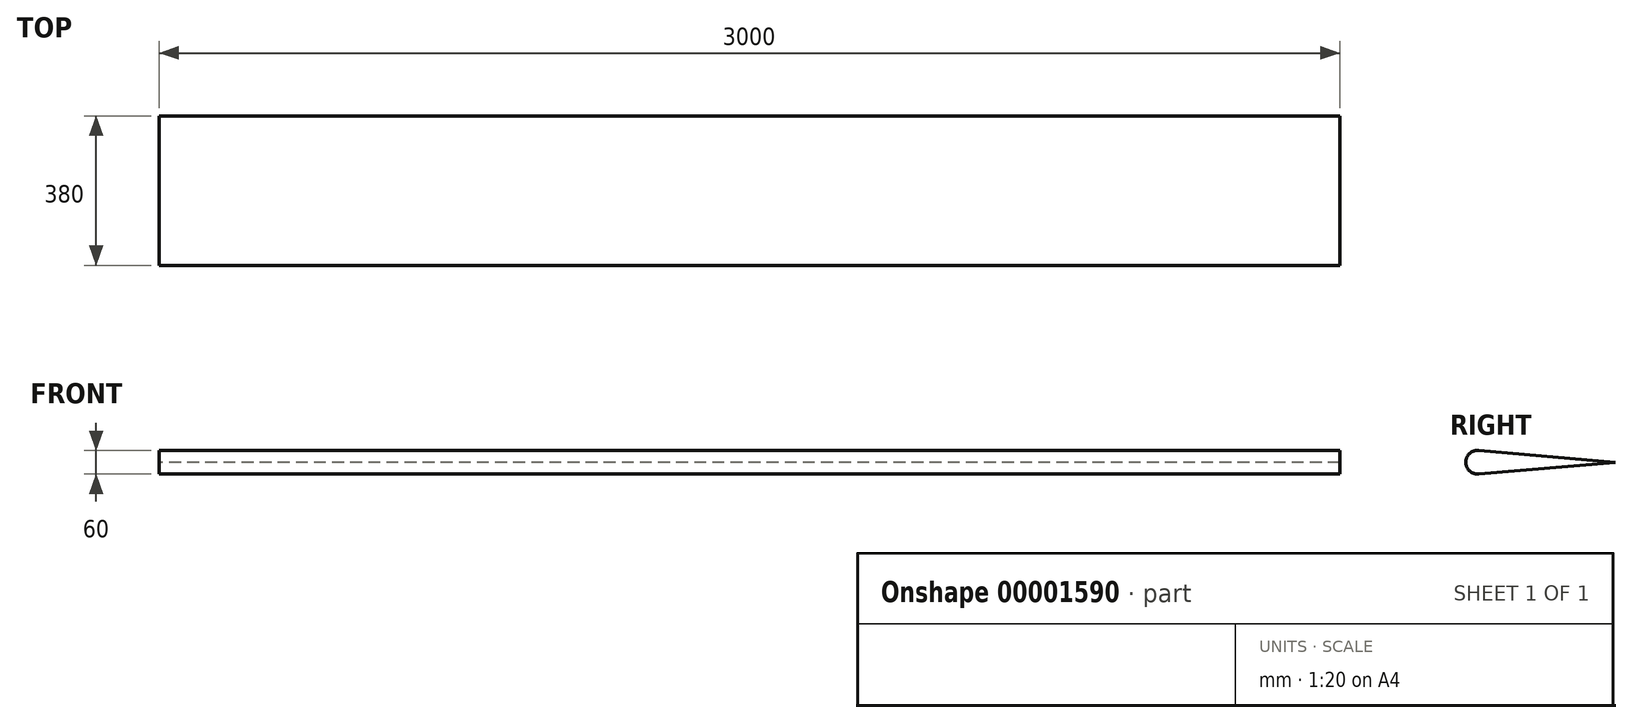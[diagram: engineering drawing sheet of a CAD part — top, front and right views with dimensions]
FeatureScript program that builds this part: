
annotation { "Feature Type Name" : "Feature", "Feature Type Description" : "" }
export const myFeature = defineFeature(function(context is Context, id is Id, definition is map)
    precondition{}
    {
        {
            var Q0;
            Q0=qCreatedBy(makeId("Right.planeOp"),FACE);
            var sketch = newSketch(context, id + "F0", { "sketchPlane" : qUnion([Q0])});
            skArc(sketch, "E0", {"start": v(2.57, 29.89) * mm, "mid": v(-30, 0) * mm, "end": v(2.57, -29.89) * mm});
            skLineSegment(sketch, "E1", {"start": v(0, 0) * mm, "end": v(350, 0) * mm, "construction": true});
            skLineSegment(sketch, "E2", {"start": v(350, 0) * mm, "end": v(0, 30.11) * mm});
            skLineSegment(sketch, "E3", {"start": v(350, 0) * mm, "end": v(0, -30.11) * mm});
            skSolve(sketch);
        }
        {
            var Q0;
            {var subQ3=sQuery(id+"F0.wireOp",EDGE,"E0");Q0=makeQuery(id+"F0.imprint","IMPRINT",FACE,{"disambiguationData":[TD([[makeQuery(id+"F0.imprint","IMPRINT",EDGE,{"derivedFrom":subQ3}),1.0]])]});}
            extrude(context, id + "F1", {"entities" : qUnion([Q0]), "endBound" : BoundingType.SYMMETRIC, "depth" : 3000 * mm});
        }
    });
